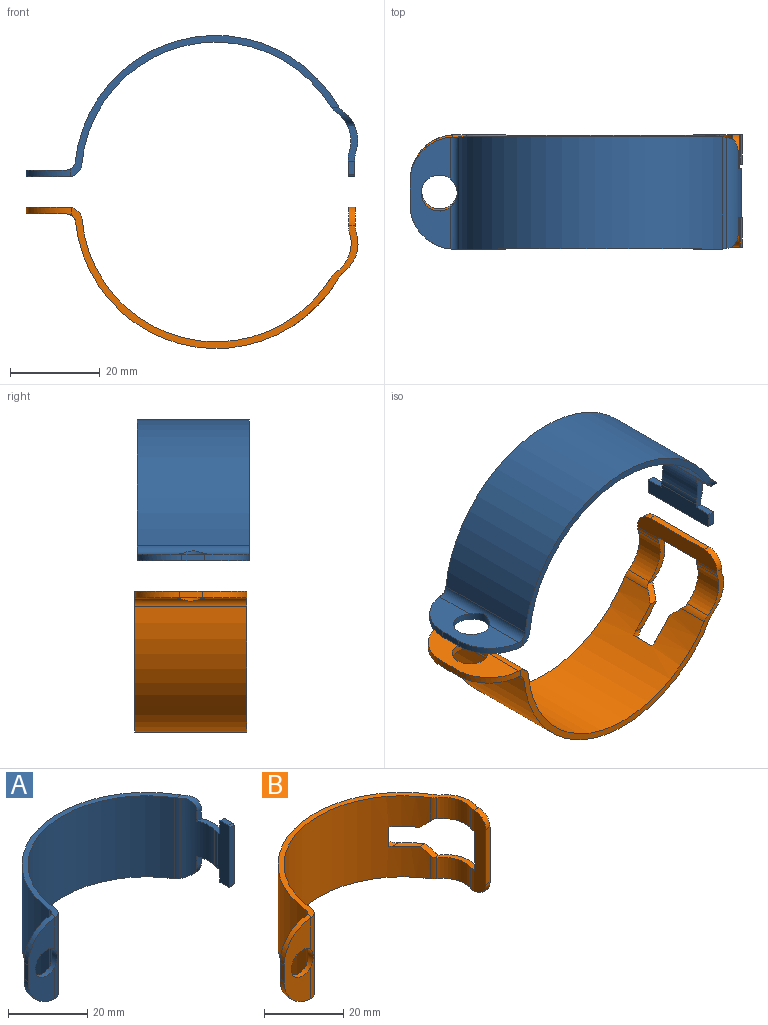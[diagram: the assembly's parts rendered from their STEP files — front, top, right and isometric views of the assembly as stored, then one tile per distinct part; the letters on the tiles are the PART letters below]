
ASSEMBLY  parts=2 mates=1
PART A: 33 faces, bbox 73.9x31.5x25 mm
  f0: plane 18x1.5mm, normal (0,-1,0), area 27mm2, adj f2,f3,f31,f32
  f1: cylinder r=8mm len=24.79mm, axis (0,0,-1), area 162mm2, adj f19,f20,f23,f24,f25,f27,f28,f29
  f2: plane 19x4.3mm, normal (-1,0,0), area 75.2mm2, adj f0,f17,f18,f20,f21,f22,f24,f29
  f3: plane 19x4.28mm, normal (1,0,0), area 75mm2, adj f0,f17,f18,f20,f21,f22,f24,f30
  f4: cylinder r=8.04mm len=24.78mm, axis (0,0,-1), area 159.4mm2, adj f19,f20,f23,f24,f25,f26,f28,f30
  f5: plane 59.74x31.45mm, normal (0,0,1), area 120.7mm2, adj f7,f8,f10,f11,f15,f25,f26,f27
  f6: plane 59.74x31.45mm, normal (0,0,-1), area 120.7mm2, adj f7,f8,f10,f11,f14,f26,f27,f28
  f7: cylinder r=3mm len=25mm, axis (0,0,-1), area 107mm2, adj f5,f6,f9,f10,f14,f15,f16
  f8: cylinder r=2mm len=25mm, axis (0,0,-1), area 66mm2, adj f5,f6,f11,f12,f14,f15,f16
  f9: plane 24.97x9.44mm, normal (0,-1,0), area 146.7mm2, adj f7,f13,f14,f15,f16
  f10: cylinder r=30mm len=55.39mm, axis (0,0,-1), area 1872.6mm2, adj f5,f6,f7,f27
  f11: cylinder r=31.5mm len=58.58mm, axis (0,0,-1), area 1978.1mm2, adj f5,f6,f8,f26
  f12: plane 24.9x8.98mm, normal (0,1,0), area 138.1mm2, adj f8,f13,f14,f15,f16
  f13: plane 5x1.5mm, normal (-1,0,0), area 7.5mm2, adj f9,f12,f14,f15
  f14: cylinder r=10mm len=10mm, axis (0,-1,0), area 23.7mm2, adj f6,f7,f8,f9,f12,f13
  f15: cylinder r=10mm len=10mm, axis (0,1,0), area 23.7mm2, adj f5,f7,f8,f9,f12,f13
  f16: cylinder r=4mm len=8mm, axis (0,-1,0), area 39.6mm2, adj f7,f8,f9,f12
  f17: plane 3x1.5mm, normal (0,0,-1), area 4.5mm2, adj f2,f3,f18,f31
  f18: plane 4x1.5mm, normal (0,1,0), area 6mm2, adj f2,f3,f17,f20
  f19: plane 3x1.58mm, normal (0,-1,0), area 4.7mm2, adj f1,f4,f20,f28
  f20: plane 8x2.34mm, normal (0,0,-1), area 12.2mm2, adj f1,f2,f3,f4,f18,f19,f29,f30
  f21: plane 3x1.5mm, normal (0,0,1), area 4.5mm2, adj f2,f3,f22,f32
  f22: plane 4x1.5mm, normal (0,1,0), area 6mm2, adj f2,f3,f21,f24
  f23: plane 3x1.58mm, normal (0,-1,0), area 4.7mm2, adj f1,f4,f24,f25
  f24: plane 8x2.34mm, normal (0,0,1), area 12.2mm2, adj f1,f2,f3,f4,f22,f23,f29,f30
  f25: cylinder r=4mm len=5.18mm, axis (-1,0,0), area 10.2mm2, adj f1,f4,f5,f23,f26,f27
  f26: cylinder r=4mm len=25mm, axis (0,0,1), area 41.2mm2, adj f4,f5,f6,f11,f25,f28
  f27: cylinder r=4mm len=25mm, axis (0,0,-1), area 41.2mm2, adj f1,f5,f6,f10,f25,f28
  f28: cylinder r=4mm len=5.18mm, axis (-1,0,0), area 10.2mm2, adj f1,f4,f6,f19,f26,f27
  f29: cylinder r=4mm len=11mm, axis (0,0,-1), area 13.8mm2, adj f1,f2,f20,f24
  f30: cylinder r=4mm len=11mm, axis (0,0,-1), area 14.1mm2, adj f3,f4,f20,f24
  f31: cylinder r=0.5mm len=1.5mm, axis (-1,0,0), area 1.2mm2, adj f0,f2,f3,f17
  f32: cylinder r=0.5mm len=1.5mm, axis (1,0,0), area 1.2mm2, adj f0,f2,f3,f21
PART B: 39 faces, bbox 74x31.5x25 mm
  f0: cylinder r=8mm len=9.05mm, axis (0,0,-1), area 66.6mm2, adj f14,f27,f35,f36
  f1: cylinder r=8.04mm len=9.02mm, axis (0,0,-1), area 65.8mm2, adj f14,f27,f37,f38
  f2: cylinder r=3mm len=25mm, axis (0,0,-1), area 107mm2, adj f4,f5,f14,f15,f16,f17,f18
  f3: cylinder r=2mm len=25mm, axis (0,0,-1), area 66mm2, adj f11,f12,f14,f15,f16,f17,f18
  f4: plane 24.97x9.44mm, normal (0,-1,0), area 146.7mm2, adj f2,f13,f16,f17,f18
  f5: cylinder r=30mm len=55.39mm, axis (0,0,-1), area 1803.4mm2, adj f2,f14,f15,f20,f21,f22,f23,f24
  f6: cylinder r=8mm len=9.05mm, axis (0,0,-1), area 66.6mm2, adj f15,f28,f31,f32
  f7: plane 25x4.3mm, normal (-1,0,0), area 97.1mm2, adj f8,f14,f15,f19,f27,f28,f29,f30
  f8: plane 17x1.5mm, normal (0,-1,0), area 25.5mm2, adj f7,f9,f29,f30
  f9: plane 25x4.28mm, normal (1,0,0), area 96.8mm2, adj f8,f14,f15,f19,f27,f28,f29,f30
  f10: cylinder r=8.04mm len=9.02mm, axis (0,0,-1), area 65.8mm2, adj f15,f28,f33,f34
  f11: cylinder r=31.5mm len=58.58mm, axis (0,0,-1), area 1896.6mm2, adj f3,f14,f15,f20,f21,f22,f23,f24
  f12: plane 24.9x8.98mm, normal (0,1,0), area 138.1mm2, adj f3,f13,f16,f17,f18
  f13: plane 5x1.5mm, normal (-1,0,0), area 7.5mm2, adj f4,f12,f16,f17
  f14: plane 63.94x31.45mm, normal (0,0,1), area 138.7mm2, adj f0,f1,f2,f3,f5,f7,f9,f11
  f15: plane 63.94x31.45mm, normal (0,0,-1), area 138.7mm2, adj f2,f3,f5,f6,f7,f9,f10,f11
  f16: cylinder r=10mm len=10mm, axis (0,-1,0), area 23.6mm2, adj f2,f3,f4,f12,f13,f15
  f17: cylinder r=10mm len=10mm, axis (0,1,0), area 23.6mm2, adj f2,f3,f4,f12,f13,f14
  f18: cylinder r=4mm len=8mm, axis (0,-1,0), area 39.6mm2, adj f2,f3,f4,f12
  f19: plane 12x1.5mm, normal (0,1,0), area 18mm2, adj f7,f9,f27,f28
  f20: plane 3.9x3.04mm, normal (0,-0.71,0.71), area 7.6mm2, adj f5,f11,f21,f28,f31,f34
  f21: plane 6.59x5mm, normal (0,0,1), area 10.1mm2, adj f5,f11,f20,f22
  f22: cylinder r=3mm len=3mm, axis (1,0,0), area 3.9mm2, adj f5,f11,f21,f26
  f23: cylinder r=3mm len=3mm, axis (1,0,0), area 3.9mm2, adj f5,f11,f24,f26
  f24: plane 6.59x5mm, normal (0,0,-1), area 10.1mm2, adj f5,f11,f23,f25
  f25: plane 3.9x3.04mm, normal (0,-0.71,-0.71), area 7.6mm2, adj f5,f11,f24,f27,f35,f38
  f26: plane 5.88x1.88mm, normal (1,0,0), area 9.4mm2, adj f5,f11,f22,f23
  f27: plane 11x5.5mm, normal (0,0,-1), area 17.2mm2, adj f0,f1,f7,f9,f19,f25,f35,f36
  f28: plane 11x5.5mm, normal (0,0,1), area 17.2mm2, adj f6,f7,f9,f10,f19,f20,f31,f32
  f29: cylinder r=4mm len=4mm, axis (1,0,0), area 9.4mm2, adj f7,f8,f9,f15
  f30: cylinder r=4mm len=4mm, axis (-1,0,0), area 9.4mm2, adj f7,f8,f9,f14
  f31: cylinder r=4mm len=7.28mm, axis (0,0,-1), area 11.1mm2, adj f5,f6,f15,f20,f28
  f32: cylinder r=4mm len=6.5mm, axis (0,0,-1), area 8.1mm2, adj f6,f7,f15,f28
  f33: cylinder r=4mm len=6.5mm, axis (0,0,-1), area 8.4mm2, adj f9,f10,f15,f28
  f34: cylinder r=4mm len=7.29mm, axis (0,0,1), area 11.1mm2, adj f10,f11,f15,f20,f28
  f35: cylinder r=4mm len=7.28mm, axis (0,0,-1), area 11.1mm2, adj f0,f5,f14,f25,f27
  f36: cylinder r=4mm len=6.5mm, axis (0,0,-1), area 8.1mm2, adj f0,f7,f14,f27
  f37: cylinder r=4mm len=6.5mm, axis (0,0,-1), area 8.4mm2, adj f1,f9,f14,f27
  f38: cylinder r=4mm len=7.29mm, axis (0,0,1), area 11.1mm2, adj f1,f11,f14,f25,f27
PLACE A rot(axis=(1,0,0),90deg) t=(66.75,-0.5,8.3)mm
PLACE B rot(axis=(-1,0,0),90deg) t=(66.82,0,1.5)mm
MATE planar A.f24 <-> B.f28  axis (0,-1,0) through (65.45,-6,13.84)mm
